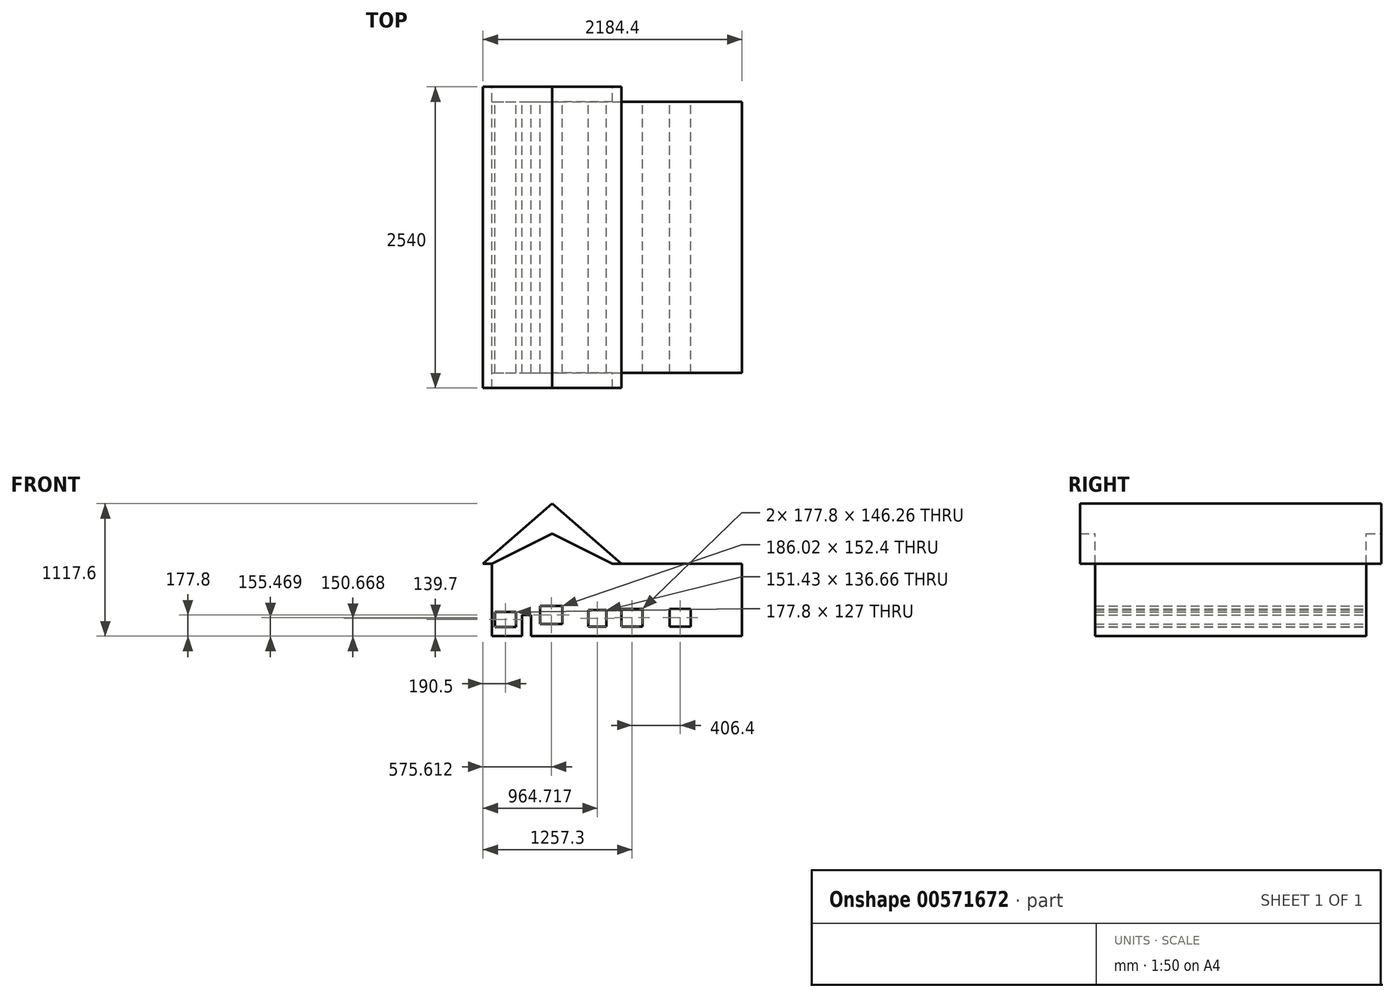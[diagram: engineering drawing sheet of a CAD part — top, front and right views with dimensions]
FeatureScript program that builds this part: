
annotation { "Feature Type Name" : "Feature", "Feature Type Description" : "" }
export const myFeature = defineFeature(function(context is Context, id is Id, definition is map)
    precondition{}
    {
        {
            var Q0;
            Q0=qCreatedBy(makeId("Front.planeOp"),FACE);
            var sketch = newSketch(context, id + "F0", { "sketchPlane" : qUnion([Q0])});
            skLineSegment(sketch, "E0", {"start": v(0, 0) * mm, "end": v(-508, 0) * mm});
            skLineSegment(sketch, "E1", {"start": v(0, 0) * mm, "end": v(508, 0) * mm});
            skLineSegment(sketch, "E2", {"start": v(0, 0) * mm, "end": v(0, 254) * mm});
            skLineSegment(sketch, "E3", {"start": v(-508, 0) * mm, "end": v(0, 254) * mm});
            skLineSegment(sketch, "E4", {"start": v(508, 0) * mm, "end": v(0, 254) * mm});
            skLineSegment(sketch, "E5", {"start": v(-508, 0) * mm, "end": v(-584.2, 0) * mm});
            skLineSegment(sketch, "E6", {"start": v(508, 0) * mm, "end": v(584.2, 0) * mm});
            skLineSegment(sketch, "E7", {"start": v(0, 254) * mm, "end": v(0, 508) * mm});
            skLineSegment(sketch, "E8", {"start": v(584.2, 0) * mm, "end": v(0, 508) * mm});
            skLineSegment(sketch, "E9", {"start": v(-584.2, 0) * mm, "end": v(0, 508) * mm});
            skLineSegment(sketch, "E10", {"start": v(-508, 0) * mm, "end": v(-508, -609.6) * mm});
            skLineSegment(sketch, "E11", {"start": v(-508, -609.6) * mm, "end": v(508, -609.6) * mm});
            skLineSegment(sketch, "E12", {"start": v(508, 0) * mm, "end": v(508, -609.6) * mm});
            skLineSegment(sketch, "E13", {"start": v(-254, -609.6) * mm, "end": v(-254, -431.8) * mm});
            skLineSegment(sketch, "E14", {"start": v(-254, -431.8) * mm, "end": v(-177.8, -431.8) * mm});
            skLineSegment(sketch, "E15", {"start": v(-177.8, -431.8) * mm, "end": v(-177.8, -609.6) * mm});
            skLineSegment(sketch, "E16", {"start": v(584.2, 0) * mm, "end": v(1600.2, 0) * mm});
            skLineSegment(sketch, "E17", {"start": v(1600.2, 0) * mm, "end": v(1600.2, -609.6) * mm});
            skLineSegment(sketch, "E18", {"start": v(508, -609.6) * mm, "end": v(1600.2, -609.6) * mm});
            skLineSegment(sketch, "E19.bottom", {"start": v(-482.6, -406.4) * mm, "end": v(-304.8, -406.4) * mm});
            skLineSegment(sketch, "E19.top", {"start": v(-482.6, -533.4) * mm, "end": v(-304.8, -533.4) * mm});
            skLineSegment(sketch, "E19.left", {"start": v(-482.6, -406.4) * mm, "end": v(-482.6, -533.4) * mm});
            skLineSegment(sketch, "E19.right", {"start": v(-304.8, -406.4) * mm, "end": v(-304.8, -533.4) * mm});
            skLineSegment(sketch, "E20.bottom", {"start": v(304.8, -390.6) * mm, "end": v(456.23, -390.6) * mm});
            skLineSegment(sketch, "E20.top", {"start": v(304.8, -527.26) * mm, "end": v(456.23, -527.26) * mm});
            skLineSegment(sketch, "E20.left", {"start": v(304.8, -390.6) * mm, "end": v(304.8, -527.26) * mm});
            skLineSegment(sketch, "E20.right", {"start": v(456.23, -390.6) * mm, "end": v(456.23, -527.26) * mm});
            skLineSegment(sketch, "E21.bottom", {"start": v(584.2, -381) * mm, "end": v(762, -381) * mm});
            skLineSegment(sketch, "E21.top", {"start": v(584.2, -527.26) * mm, "end": v(762, -527.26) * mm});
            skLineSegment(sketch, "E21.left", {"start": v(584.2, -381) * mm, "end": v(584.2, -527.26) * mm});
            skLineSegment(sketch, "E21.right", {"start": v(762, -381) * mm, "end": v(762, -527.26) * mm});
            skLineSegment(sketch, "E22.bottom", {"start": v(990.6, -381) * mm, "end": v(1168.4, -381) * mm});
            skLineSegment(sketch, "E22.top", {"start": v(990.6, -527.26) * mm, "end": v(1168.4, -527.26) * mm});
            skLineSegment(sketch, "E22.left", {"start": v(990.6, -381) * mm, "end": v(990.6, -527.26) * mm});
            skLineSegment(sketch, "E22.right", {"start": v(1168.4, -381) * mm, "end": v(1168.4, -527.26) * mm});
            skLineSegment(sketch, "E23.bottom", {"start": v(-101.6, -355.6) * mm, "end": v(84.42, -355.6) * mm});
            skLineSegment(sketch, "E23.top", {"start": v(-101.6, -508) * mm, "end": v(84.42, -508) * mm});
            skLineSegment(sketch, "E23.left", {"start": v(-101.6, -355.6) * mm, "end": v(-101.6, -508) * mm});
            skLineSegment(sketch, "E23.right", {"start": v(84.42, -355.6) * mm, "end": v(84.42, -508) * mm});
            skText(sketch, "E24", { "text": "Maddie\'s house ", "fontName": "OpenSans-Regular.ttf"});
            const initialGuessF0  = {"E24": [-0.6374, 0.72609, 1, 0, 0.14866]};
            skSetInitialGuess(sketch, initialGuessF0);
            skSolve(sketch);
        }
        {
            var Q0;
            Q0=makeQuery(id+"F0.imprint","IMPRINT",FACE,{"disambiguationData":[TD([[makeQuery(id+"F0.imprint","IMPRINT",EDGE,{"derivedFrom":sQuery(id+"F0.wireOp",EDGE,"E3")}),1.0]])]});
            var Q1;
            Q1=makeQuery(id+"F0.imprint","IMPRINT",FACE,{"disambiguationData":[TD([[makeQuery(id+"F0.imprint","IMPRINT",EDGE,{"derivedFrom":sQuery(id+"F0.wireOp",EDGE,"E4")}),-1.0]])]});
            extrude(context, id + "F1", {"entities" : qUnion([Q0, Q1]), "endBound" : BoundingType.SYMMETRIC, "depth" : 2540 * mm, "offsetDistance" : 25.4 * mm});
        }
        {
            var Q0;
            Q0=makeQuery(id+"F0.imprint","IMPRINT",FACE,{"disambiguationData":[TD([[makeQuery(id+"F0.imprint","IMPRINT",EDGE,{"derivedFrom":sQuery(id+"F0.wireOp",EDGE,"E3")}),1.0]])]});
            var Q1;
            Q1=makeQuery(id+"F0.imprint","IMPRINT",FACE,{"disambiguationData":[TD([[makeQuery(id+"F0.imprint","IMPRINT",EDGE,{"derivedFrom":sQuery(id+"F0.wireOp",EDGE,"E4")}),-1.0]])]});
            var Q2;
            Q2=makeQuery(id+"F0.imprint","IMPRINT",FACE,{"disambiguationData":[TD([[makeQuery(id+"F0.imprint","IMPRINT",EDGE,{"derivedFrom":sQuery(id+"F0.wireOp",EDGE,"E1")}),1.0]])]});
            var Q3;
            Q3=makeQuery(id+"F0.imprint","IMPRINT",FACE,{"disambiguationData":[TD([[makeQuery(id+"F0.imprint","IMPRINT",EDGE,{"derivedFrom":sQuery(id+"F0.wireOp",EDGE,"E0")}),-1.0]])]});
            var Q4;
            Q4=makeQuery(id+"F0.imprint","IMPRINT",FACE,{"disambiguationData":[TD([[makeQuery(id+"F0.imprint","IMPRINT",EDGE,{"derivedFrom":sQuery(id+"F0.wireOp",EDGE,"E0")}),1.0]])]});
            var Q5;
            Q5=makeQuery(id+"F0.imprint","IMPRINT",FACE,{"disambiguationData":[TD([[makeQuery(id+"F0.imprint","IMPRINT",EDGE,{"derivedFrom":sQuery(id+"F0.wireOp",EDGE,"E6")}),-1.0]])]});
            extrude(context, id + "F2", {"entities" : qUnion([Q0, Q1, Q2, Q3, Q4, Q5]), "operationType" : NewBodyOperationType.ADD, "endBound" : BoundingType.SYMMETRIC, "depth" : 2286 * mm, "offsetDistance" : 25.4 * mm});
        }
    });
